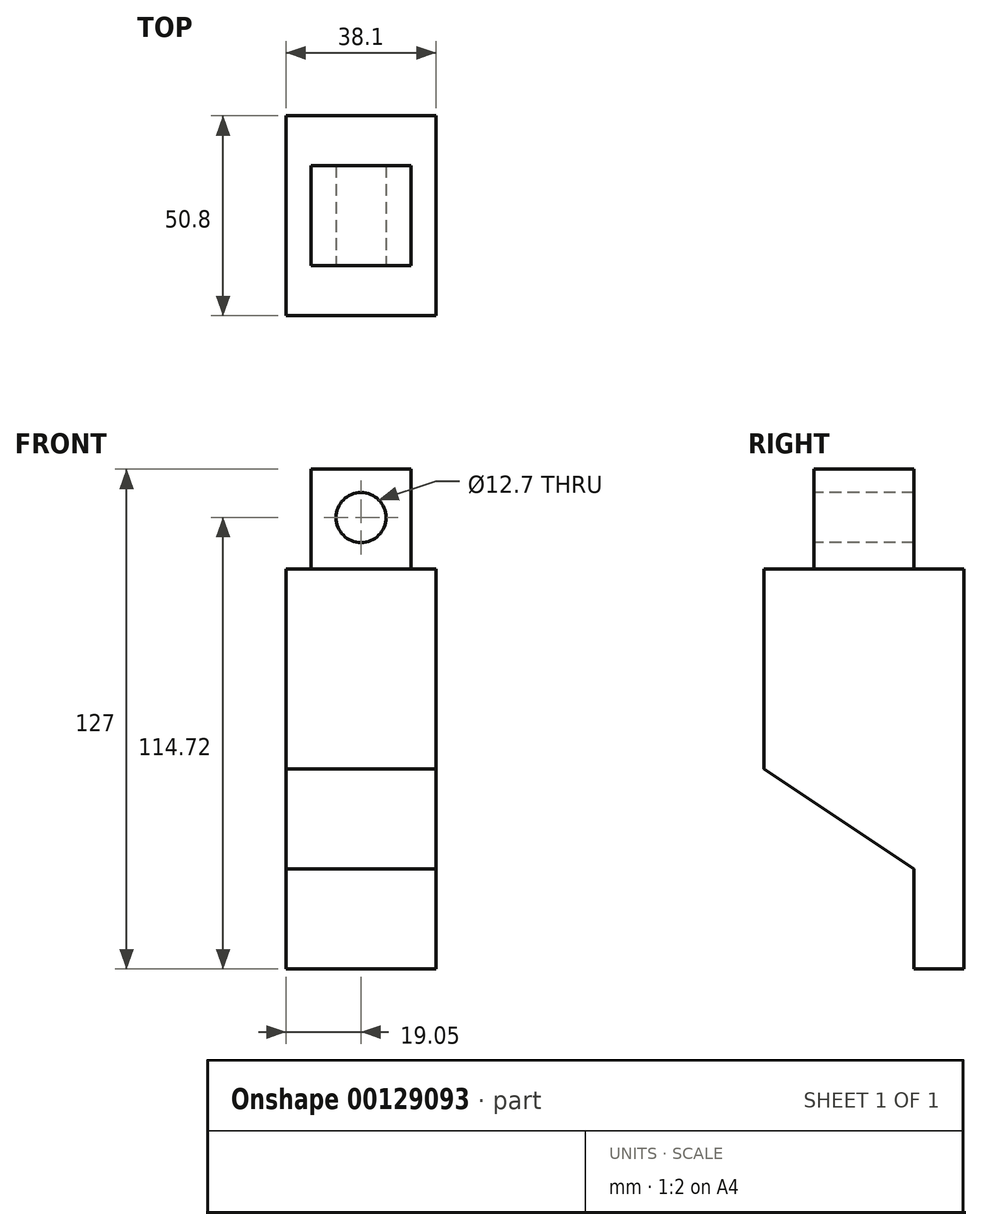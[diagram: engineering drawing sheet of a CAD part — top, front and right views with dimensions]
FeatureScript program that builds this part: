
annotation { "Feature Type Name" : "Feature", "Feature Type Description" : "" }
export const myFeature = defineFeature(function(context is Context, id is Id, definition is map)
    precondition{}
    {
        {
            var Q0;
            Q0=qCreatedBy(makeId("Front.planeOp"),FACE);
            var sketch = newSketch(context, id + "F0", { "sketchPlane" : qUnion([Q0])});
            skLineSegment(sketch, "E0.bottom", {"start": v(-19.05, 38.1) * mm, "end": v(19.05, 38.1) * mm});
            skLineSegment(sketch, "E0.top", {"start": v(-19.05, -38.1) * mm, "end": v(19.05, -38.1) * mm});
            skLineSegment(sketch, "E0.left", {"start": v(-19.05, 38.1) * mm, "end": v(-19.05, -38.1) * mm});
            skLineSegment(sketch, "E0.right", {"start": v(19.05, 38.1) * mm, "end": v(19.05, -38.1) * mm});
            skPoint(sketch, "E0.middle", {"position": v(0, 0) * mm});
            skSolve(sketch);
        }
        {
            var Q0;
            Q0=makeQuery(id+"F0.imprint","IMPRINT",FACE,{"disambiguationData":[TD([[makeQuery(id+"F0.imprint","IMPRINT",EDGE,{"derivedFrom":sQuery(id+"F0.wireOp",EDGE,"E0.bottom")}),-1.0]])]});
            extrude(context, id + "F1", {"entities" : qUnion([Q0]), "endBound" : BoundingType.SYMMETRIC, "depth" : 50.8 * mm});
        }
        {
            var Q0;
            Q0=makeQuery(id+"F1.opExtrude","CAP_EDGE",EDGE,{"disambiguationData":[OSD([sQuery(id+"F0.wireOp",EDGE,"E0.top")])],"isStart":false});
            chamfer(context, id + "F2", {"entities" : qUnion([Q0]), "chamferType" : ChamferType.TWO_OFFSETS, "width1" : 25.4 * mm, "oppositeDirection" : false, "width2" : 38.1 * mm, "tangentPropagation" : true});
        }
        {
            var Q0;
            Q0=makeQuery(id+"F1.opExtrude","SWEPT_FACE",FACE,{"disambiguationData":[OSD([sQuery(id+"F0.wireOp",EDGE,"E0.bottom")])]});
            var sketch = newSketch(context, id + "F3", { "sketchPlane" : qUnion([Q0])});
            skLineSegment(sketch, "E1.bottom", {"start": v(12.7, -12.7) * mm, "end": v(-12.7, -12.7) * mm});
            skLineSegment(sketch, "E1.top", {"start": v(12.7, 12.7) * mm, "end": v(-12.7, 12.7) * mm});
            skLineSegment(sketch, "E1.left", {"start": v(12.7, -12.7) * mm, "end": v(12.7, 12.7) * mm});
            skLineSegment(sketch, "E1.right", {"start": v(-12.7, -12.7) * mm, "end": v(-12.7, 12.7) * mm});
            skPoint(sketch, "E1.middle", {"position": v(0, 0) * mm});
            skSolve(sketch);
        }
        {
            var Q0;
            Q0=makeQuery(id+"F3.imprint","IMPRINT",FACE,{"disambiguationData":[TD([[makeQuery(id+"F3.imprint","IMPRINT",EDGE,{"derivedFrom":sQuery(id+"F3.wireOp",EDGE,"E1.bottom")}),-1.0]])]});
            extrude(context, id + "F4", {"entities" : qUnion([Q0]), "operationType" : NewBodyOperationType.ADD, "depth" : 25.4 * mm});
        }
        {
            var Q0;
            Q0=makeQuery(id+"F4.opExtrude","SWEPT_FACE",FACE,{"disambiguationData":[OSD([sQuery(id+"F3.wireOp",EDGE,"E1.bottom")])]});
            var sketch = newSketch(context, id + "F5", { "sketchPlane" : qUnion([Q0])});
            skCircle(sketch, "E2", {"center": v(0, 51.22) * mm, "radius": 6.35 * mm});
            skSolve(sketch);
        }
        {
            var Q0;
            Q0 = qSketchRegion(id + "F5", true);
            extrude(context, id + "F6", {"entities" : qUnion([Q0]), "operationType" : NewBodyOperationType.REMOVE, "oppositeDirection" : true, "depth" : 25.4 * mm});
        }
        {
            var Q0;
            Q0=makeQuery(id+"F1.opExtrude","SWEPT_FACE",FACE,{"disambiguationData":[OSD([sQuery(id+"F0.wireOp",EDGE,"E0.top")])]});
            var sketch = newSketch(context, id + "F7", { "sketchPlane" : qUnion([Q0])});
            skLineSegment(sketch, "E3.bottom", {"start": v(-19.05, -25.4) * mm, "end": v(19.05, -25.4) * mm});
            skLineSegment(sketch, "E3.top", {"start": v(-19.05, -12.7) * mm, "end": v(19.05, -12.7) * mm});
            skLineSegment(sketch, "E3.left", {"start": v(-19.05, -25.4) * mm, "end": v(-19.05, -12.7) * mm});
            skLineSegment(sketch, "E3.right", {"start": v(19.05, -25.4) * mm, "end": v(19.05, -12.7) * mm});
            skSolve(sketch);
        }
        {
            var Q0;
            Q0=makeQuery(id+"F7.imprint","IMPRINT",FACE,{"disambiguationData":[TD([[makeQuery(id+"F7.imprint","IMPRINT",EDGE,{"derivedFrom":sQuery(id+"F7.wireOp",EDGE,"E3.bottom")}),1.0]])]});
            extrude(context, id + "F8", {"entities" : qUnion([Q0]), "operationType" : NewBodyOperationType.ADD, "depth" : 25.4 * mm});
        }
    });
